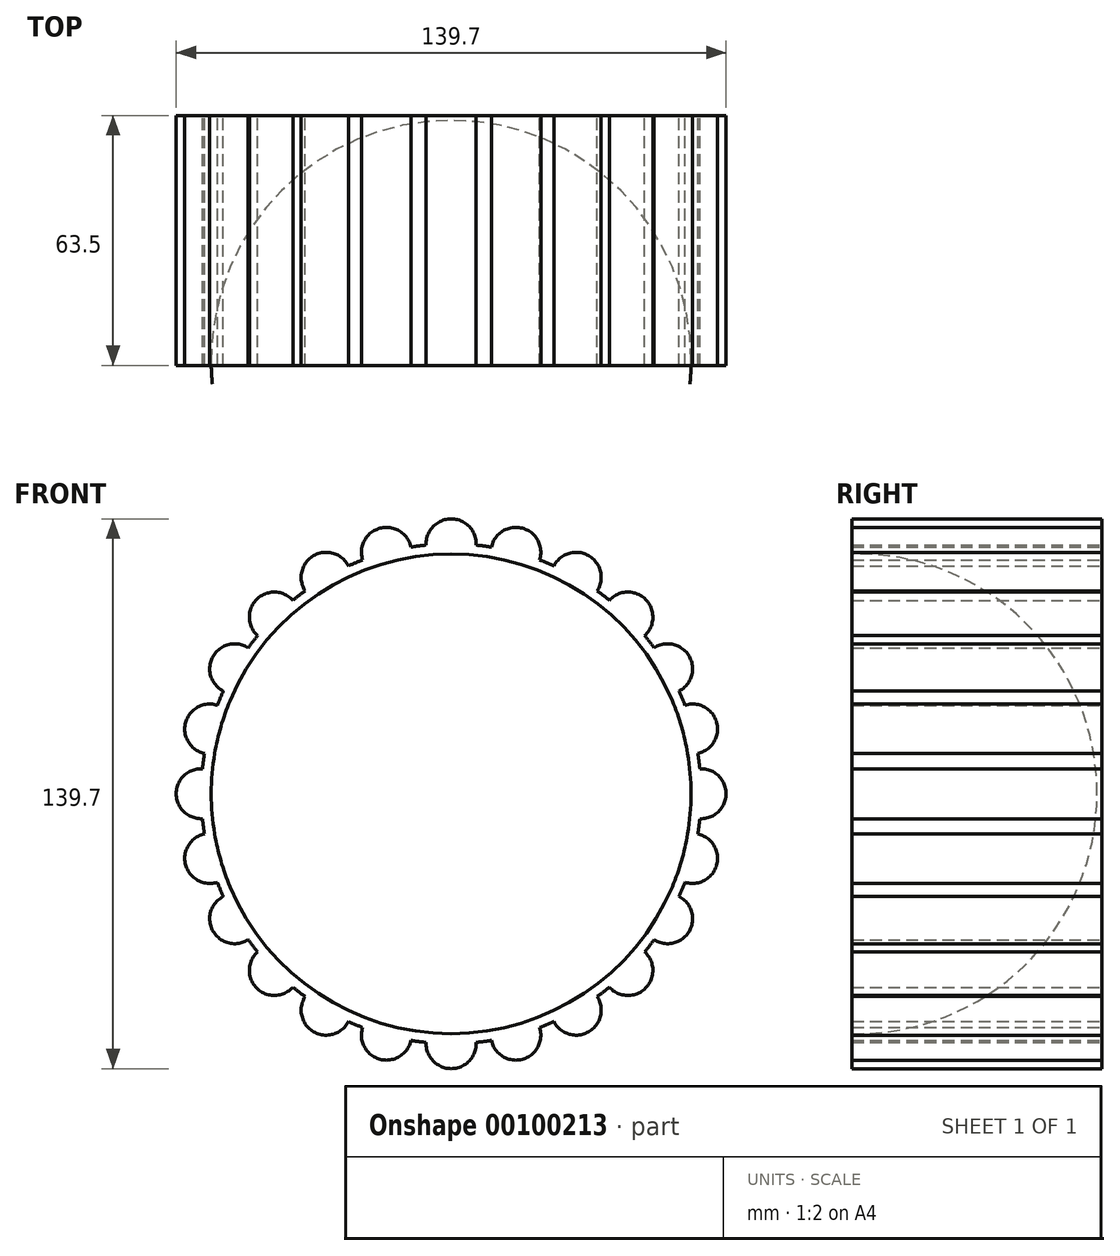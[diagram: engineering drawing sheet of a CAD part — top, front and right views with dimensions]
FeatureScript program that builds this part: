
annotation { "Feature Type Name" : "Feature", "Feature Type Description" : "" }
export const myFeature = defineFeature(function(context is Context, id is Id, definition is map)
    precondition{}
    {
        {
            var Q0;
            Q0=qCreatedBy(makeId("Front.planeOp"),FACE);
            var sketch = newSketch(context, id + "F0", { "sketchPlane" : qUnion([Q0])});
            skCircle(sketch, "E0", {"center": v(-63.5, 0) * mm, "radius": 6.35 * mm});
            skCircle(sketch, "E1.1.0", {"center": v(-61.34, 16.44) * mm, "radius": 6.35 * mm});
            skCircle(sketch, "E1.2.0", {"center": v(-55, 31.75) * mm, "radius": 6.35 * mm});
            skCircle(sketch, "E1.3.0", {"center": v(-44.9, 44.9) * mm, "radius": 6.35 * mm});
            skCircle(sketch, "E1.4.0", {"center": v(-31.75, 55) * mm, "radius": 6.35 * mm});
            skCircle(sketch, "E1.5.0", {"center": v(-16.44, 61.34) * mm, "radius": 6.35 * mm});
            skCircle(sketch, "E1.6.0", {"center": v(0, 63.5) * mm, "radius": 6.35 * mm});
            skCircle(sketch, "E1.7.0", {"center": v(16.44, 61.34) * mm, "radius": 6.35 * mm});
            skCircle(sketch, "E1.8.0", {"center": v(31.75, 55) * mm, "radius": 6.35 * mm});
            skCircle(sketch, "E1.9.0", {"center": v(44.9, 44.9) * mm, "radius": 6.35 * mm});
            skCircle(sketch, "E1.10.0", {"center": v(55, 31.75) * mm, "radius": 6.35 * mm});
            skCircle(sketch, "E1.11.0", {"center": v(61.34, 16.44) * mm, "radius": 6.35 * mm});
            skCircle(sketch, "E1.12.0", {"center": v(63.5, 0) * mm, "radius": 6.35 * mm});
            skCircle(sketch, "E1.13.0", {"center": v(61.34, -16.44) * mm, "radius": 6.35 * mm});
            skCircle(sketch, "E1.14.0", {"center": v(55, -31.75) * mm, "radius": 6.35 * mm});
            skCircle(sketch, "E1.15.0", {"center": v(44.9, -44.9) * mm, "radius": 6.35 * mm});
            skCircle(sketch, "E1.16.0", {"center": v(31.75, -55) * mm, "radius": 6.35 * mm});
            skCircle(sketch, "E1.17.0", {"center": v(16.44, -61.34) * mm, "radius": 6.35 * mm});
            skCircle(sketch, "E1.18.0", {"center": v(0, -63.5) * mm, "radius": 6.35 * mm});
            skCircle(sketch, "E1.19.0", {"center": v(-16.44, -61.34) * mm, "radius": 6.35 * mm});
            skCircle(sketch, "E1.20.0", {"center": v(-31.75, -55) * mm, "radius": 6.35 * mm});
            skCircle(sketch, "E1.21.0", {"center": v(-44.9, -44.9) * mm, "radius": 6.35 * mm});
            skCircle(sketch, "E1.22.0", {"center": v(-55, -31.75) * mm, "radius": 6.35 * mm});
            skCircle(sketch, "E1.23.0", {"center": v(-61.34, -16.44) * mm, "radius": 6.35 * mm});
            skPoint(sketch, "E1.center", {"position": v(0, 0) * mm});
            skLineSegment(sketch, "E1.anchor1", {"start": v(0, 0) * mm, "end": v(-63.5, 0) * mm, "construction": true});
            skLineSegment(sketch, "E1.anchor2", {"start": v(0, 0) * mm, "end": v(-61.34, -16.44) * mm, "construction": true});
            skCircle(sketch, "E2", {"center": v(0, 0) * mm, "radius": 63.5 * mm});
            skSolve(sketch);
        }
        {
            var Q0;
            Q0 = qSketchRegion(id + "F0", true);
            extrude(context, id + "F1", {"entities" : qUnion([Q0]), "endBound" : BoundingType.SYMMETRIC, "depth" : 63.5 * mm});
        }
        {
            var Q0;
            Q0=qCreatedBy(makeId("Front.planeOp"),FACE);
            cPlane(context, id + "F2", {"entities" : qUnion([Q0]), "cplaneType" : CPlaneType.OFFSET, "offset" : 30.48 * mm, "width" : 152.4 * mm, "height" : 152.4 * mm});
        }
        {
            var Q0;
            Q0=qCreatedBy(id+"F2.planeOp",FACE);
            var sketch = newSketch(context, id + "F3", { "sketchPlane" : qUnion([Q0])});
            skLineSegment(sketch, "E3", {"start": v(-67.35, 0) * mm, "end": v(65.65, 0) * mm});
            skArc(sketch, "E4", {"start": v(-60.96, 0) * mm, "mid": v(0, 60.96) * mm, "end": v(60.96, 0) * mm});
            skSolve(sketch);
        }
        {
            var Q0;
            Q0 = qSketchRegion(id + "F3", true);
            var Q1;
            Q1=sQuery(id+"F3.wireOp",EDGE,"E3");
            revolve(context, id + "F4", {"entities" : qUnion([Q0]), "axis" : qUnion([Q1]), "revolveType" : RevolveType.FULL});
        }
        {
            var Q0;
            Q0=makeQuery(id+"F4.opRevolve","SWEPT_BODY",BODY,{"disambiguationData":[OSD([sQuery(id+"F3.wireOp",EDGE,"E3"),sQuery(id+"F3.wireOp",EDGE,"E4")])]});
            var Q1;
            Q1=makeQuery(id+"F1.opExtrude","SWEPT_BODY",BODY,{"disambiguationData":[OSD([sQuery(id+"F0.wireOp",EDGE,"E0"),sQuery(id+"F0.wireOp",EDGE,"E1.1.0"),sQuery(id+"F0.wireOp",EDGE,"E1.2.0"),sQuery(id+"F0.wireOp",EDGE,"E1.3.0"),sQuery(id+"F0.wireOp",EDGE,"E1.4.0"),sQuery(id+"F0.wireOp",EDGE,"E1.5.0"),sQuery(id+"F0.wireOp",EDGE,"E1.6.0"),sQuery(id+"F0.wireOp",EDGE,"E1.7.0"),sQuery(id+"F0.wireOp",EDGE,"E1.8.0"),sQuery(id+"F0.wireOp",EDGE,"E1.9.0"),sQuery(id+"F0.wireOp",EDGE,"E1.10.0"),sQuery(id+"F0.wireOp",EDGE,"E1.11.0"),sQuery(id+"F0.wireOp",EDGE,"E1.12.0"),sQuery(id+"F0.wireOp",EDGE,"E1.13.0"),sQuery(id+"F0.wireOp",EDGE,"E1.14.0"),sQuery(id+"F0.wireOp",EDGE,"E1.15.0"),sQuery(id+"F0.wireOp",EDGE,"E1.16.0"),sQuery(id+"F0.wireOp",EDGE,"E1.17.0"),sQuery(id+"F0.wireOp",EDGE,"E1.18.0"),sQuery(id+"F0.wireOp",EDGE,"E1.19.0"),sQuery(id+"F0.wireOp",EDGE,"E1.20.0"),sQuery(id+"F0.wireOp",EDGE,"E1.21.0"),sQuery(id+"F0.wireOp",EDGE,"E1.22.0"),sQuery(id+"F0.wireOp",EDGE,"E1.23.0"),sQuery(id+"F0.wireOp",EDGE,"E2")])]});
            booleanBodies(context, id + "F5", {"operationType" : BooleanOperationType.SUBTRACTION, "tools" : qUnion([Q0]), "targets" : qUnion([Q1])});
        }
    });
